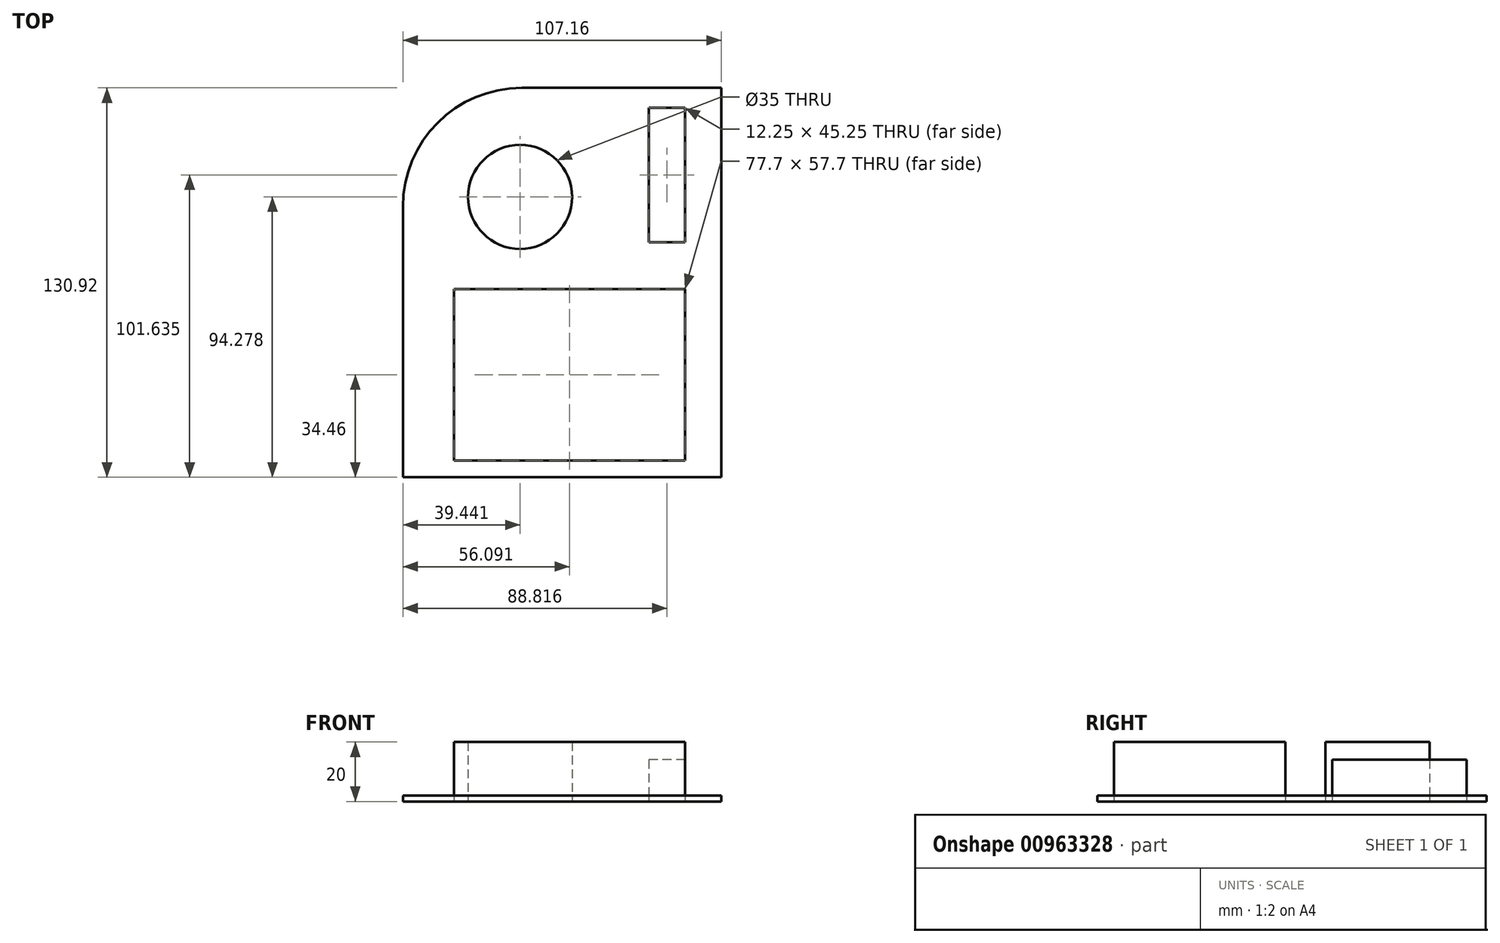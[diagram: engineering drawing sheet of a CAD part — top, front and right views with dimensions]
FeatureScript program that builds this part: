
annotation { "Feature Type Name" : "Feature", "Feature Type Description" : "" }
export const myFeature = defineFeature(function(context is Context, id is Id, definition is map)
    precondition{}
    {
        {
            var Q0;
            Q0=qCreatedBy(makeId("Top.planeOp"),FACE);
            var sketch = newSketch(context, id + "F0", { "sketchPlane" : qUnion([Q0])});
            skLineSegment(sketch, "E0.bottom", {"start": v(-64.56, -31.44) * mm, "end": v(13.14, -31.44) * mm});
            skLineSegment(sketch, "E0.top", {"start": v(-64.56, 26.26) * mm, "end": v(13.14, 26.26) * mm});
            skLineSegment(sketch, "E0.left", {"start": v(-64.56, -31.44) * mm, "end": v(-64.56, 26.26) * mm});
            skLineSegment(sketch, "E0.right", {"start": v(13.14, -31.44) * mm, "end": v(13.14, 26.26) * mm});
            skLineSegment(sketch, "E1", {"start": v(13.14, 26.26) * mm, "end": v(13.14, 41.96) * mm, "construction": true});
            skLineSegment(sketch, "E2.bottom", {"start": v(13.14, 41.96) * mm, "end": v(0.9, 41.96) * mm});
            skLineSegment(sketch, "E2.top", {"start": v(13.14, 87.2) * mm, "end": v(0.9, 87.2) * mm});
            skLineSegment(sketch, "E2.left", {"start": v(13.14, 41.96) * mm, "end": v(13.14, 87.2) * mm});
            skLineSegment(sketch, "E2.right", {"start": v(0.9, 41.96) * mm, "end": v(0.9, 87.2) * mm});
            skLineSegment(sketch, "E3", {"start": v(0.9, 41.96) * mm, "end": v(-24.86, 41.96) * mm, "construction": true});
            skCircle(sketch, "E4", {"center": v(-42.36, 57.23) * mm, "radius": 17.5 * mm});
            skPoint(sketch, "E4.first.point", {"position": v(-42.36, 39.73) * mm});
            skPoint(sketch, "E4.second.point", {"position": v(-42.36, 74.73) * mm});
            skPoint(sketch, "E4.third.point", {"position": v(-24.86, 57.23) * mm});
            skLineSegment(sketch, "E5.bottom", {"start": v(25.36, -37.05) * mm, "end": v(-81.8, -37.05) * mm});
            skLineSegment(sketch, "E5.top", {"start": v(25.36, 93.87) * mm, "end": v(-41.8, 93.87) * mm});
            skLineSegment(sketch, "E5.left", {"start": v(25.36, -37.05) * mm, "end": v(25.36, 93.87) * mm});
            skLineSegment(sketch, "E5.right", {"start": v(-81.8, -37.05) * mm, "end": v(-81.8, 53.87) * mm});
            skPoint(sketch, "E6.visualSharp", {"position": v(-81.8, 93.87) * mm});
            skArc(sketch, "E6.filletArc", {"start": v(-41.8, 93.87) * mm, "mid": v(-70.08, 82.16) * mm, "end": v(-81.8, 53.87) * mm});
            skSolve(sketch);
        }
        {
            var Q0;
            Q0=makeQuery(id+"F0.imprint","IMPRINT",FACE,{"disambiguationData":[TD([[makeQuery(id+"F0.imprint","IMPRINT",EDGE,{"derivedFrom":sQuery(id+"F0.wireOp",EDGE,"E4")}),1.0]])]});
            extrude(context, id + "F1", {"entities" : qUnion([Q0]), "depth" : 20 * mm, "offsetDistance" : 25 * mm});
        }
        {
            var Q0;
            Q0=makeQuery(id+"F0.imprint","IMPRINT",FACE,{"disambiguationData":[TD([[makeQuery(id+"F0.imprint","IMPRINT",EDGE,{"derivedFrom":sQuery(id+"F0.wireOp",EDGE,"E2.bottom")}),-1.0]])]});
            extrude(context, id + "F2", {"entities" : qUnion([Q0]), "depth" : 14 * mm, "offsetDistance" : 25 * mm});
        }
        {
            var Q0;
            Q0=makeQuery(id+"F0.imprint","IMPRINT",FACE,{"disambiguationData":[TD([[makeQuery(id+"F0.imprint","IMPRINT",EDGE,{"derivedFrom":sQuery(id+"F0.wireOp",EDGE,"E0.bottom")}),1.0]])]});
            extrude(context, id + "F3", {"entities" : qUnion([Q0]), "depth" : 20 * mm, "offsetDistance" : 25 * mm});
        }
        {
            var Q0;
            Q0=makeQuery(id+"F0.imprint","IMPRINT",FACE,{"disambiguationData":[TD([[makeQuery(id+"F0.imprint","IMPRINT",EDGE,{"derivedFrom":sQuery(id+"F0.wireOp",EDGE,"E0.bottom")}),-1.0]])]});
            extrude(context, id + "F4", {"entities" : qUnion([Q0]), "depth" : 2 * mm, "offsetDistance" : 25 * mm});
        }
    });
